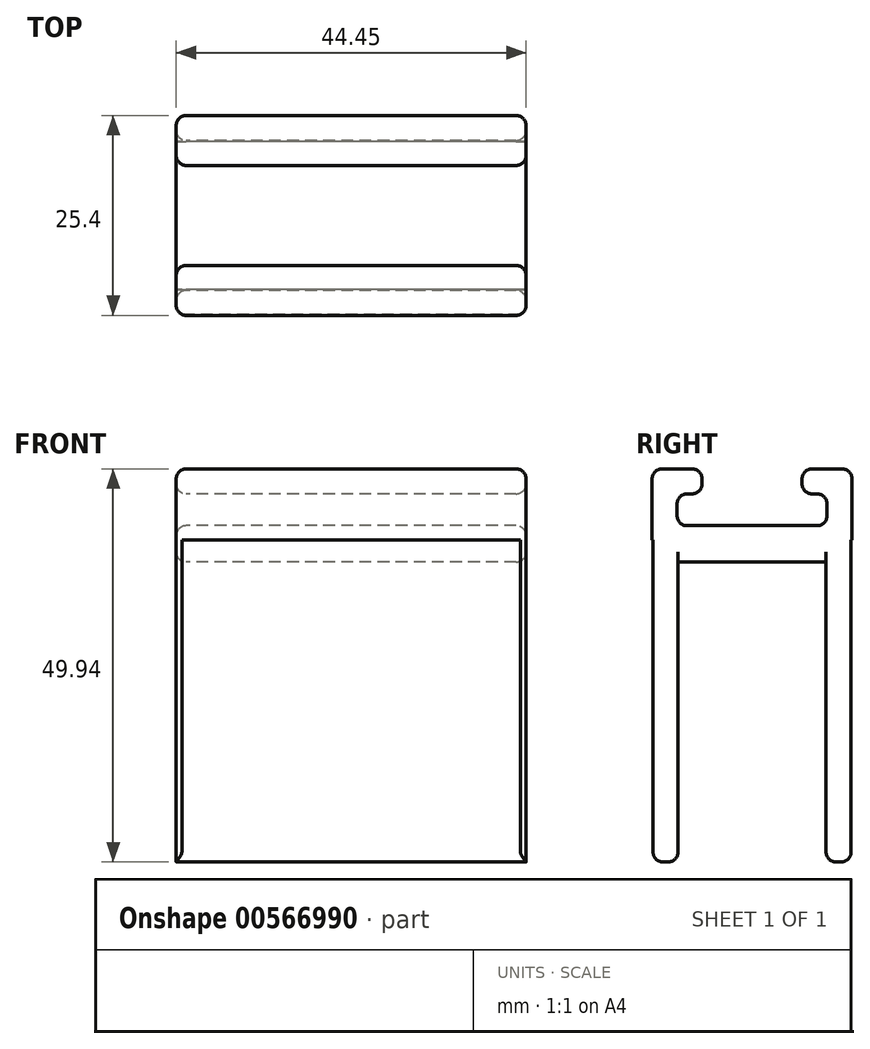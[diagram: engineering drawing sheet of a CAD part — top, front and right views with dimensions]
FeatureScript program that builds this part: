
annotation { "Feature Type Name" : "Feature", "Feature Type Description" : "" }
export const myFeature = defineFeature(function(context is Context, id is Id, definition is map)
    precondition{}
    {
        {
            var Q0;
            Q0=qCreatedBy(makeId("Right.planeOp"),FACE);
            var sketch = newSketch(context, id + "F0", { "sketchPlane" : qUnion([Q0])});
            skLineSegment(sketch, "E0.bottom", {"start": v(11.3, -24.97) * mm, "end": v(10.67, -24.97) * mm});
            skLineSegment(sketch, "E0.top", {"start": v(11.43, 24.97) * mm, "end": v(7.62, 24.97) * mm});
            skLineSegment(sketch, "E0.left", {"start": v(12.57, -23.7) * mm, "end": v(12.57, 15.95) * mm});
            skLineSegment(sketch, "E0.right", {"start": v(-12.57, -23.7) * mm, "end": v(-12.57, 15.95) * mm});
            skPoint(sketch, "E0.middle", {"position": v(0, 0) * mm});
            skLineSegment(sketch, "E1.top", {"start": v(-9.4, 13.13) * mm, "end": v(9.4, 13.13) * mm});
            skLineSegment(sketch, "E1.left", {"start": v(-9.4, -23.7) * mm, "end": v(-9.4, 13.13) * mm});
            skLineSegment(sketch, "E1.right", {"start": v(9.4, -23.7) * mm, "end": v(9.4, 13.13) * mm});
            skLineSegment(sketch, "E2.trimOffspring", {"start": v(-10.67, -24.97) * mm, "end": v(-11.3, -24.97) * mm});
            skLineSegment(sketch, "E3.bottom", {"start": v(8.26, 17.75) * mm, "end": v(-8.26, 17.75) * mm});
            skLineSegment(sketch, "E3.top", {"start": v(8.26, 21.8) * mm, "end": v(7.62, 21.8) * mm});
            skLineSegment(sketch, "E3.left", {"start": v(9.53, 19.02) * mm, "end": v(9.53, 20.52) * mm});
            skLineSegment(sketch, "E3.right", {"start": v(-9.53, 19.02) * mm, "end": v(-9.53, 20.52) * mm});
            skPoint(sketch, "E3.middle", {"position": v(0, 19.77) * mm});
            skPoint(sketch, "E3.middle.positionSnap0", {"position": v(0, 13.13) * mm});
            skPoint(sketch, "E3.centerSnap0", {"position": v(0, 13.13) * mm});
            skLineSegment(sketch, "E4.left", {"start": v(6.35, 23.7) * mm, "end": v(6.35, 23.06) * mm});
            skLineSegment(sketch, "E4.right", {"start": v(-6.35, 23.7) * mm, "end": v(-6.35, 23.06) * mm});
            skPoint(sketch, "E4.middle", {"position": v(0, 21.8) * mm});
            skLineSegment(sketch, "E5.trimOffspring", {"start": v(-7.62, 21.8) * mm, "end": v(-8.26, 21.8) * mm});
            skLineSegment(sketch, "E6.trimOffspring", {"start": v(-7.62, 24.97) * mm, "end": v(-11.43, 24.97) * mm});
            skPoint(sketch, "E4.top.end.orphan", {"position": v(-6.35, 18.62) * mm});
            skPoint(sketch, "E7.orphan", {"position": v(6.35, 18.62) * mm});
            skLineSegment(sketch, "E8.top", {"start": v(-12.7, 15.95) * mm, "end": v(-12.57, 15.95) * mm});
            skLineSegment(sketch, "E8.right", {"start": v(-12.7, 23.7) * mm, "end": v(-12.7, 15.95) * mm});
            skPoint(sketch, "E9.orphan", {"position": v(-12.57, 24.97) * mm});
            skLineSegment(sketch, "E10.top", {"start": v(12.7, 15.95) * mm, "end": v(12.57, 15.95) * mm});
            skLineSegment(sketch, "E10.right", {"start": v(12.7, 23.7) * mm, "end": v(12.7, 15.95) * mm});
            skPoint(sketch, "E11.orphan", {"position": v(12.57, 24.97) * mm});
            skPoint(sketch, "E12.visualSharp", {"position": v(-6.35, 21.8) * mm});
            skArc(sketch, "E12.filletArc", {"start": v(-7.62, 21.8) * mm, "mid": v(-6.72, 22.16) * mm, "end": v(-6.35, 23.06) * mm});
            skPoint(sketch, "E13.visualSharp", {"position": v(6.35, 21.8) * mm});
            skArc(sketch, "E13.filletArc", {"start": v(6.35, 23.06) * mm, "mid": v(6.72, 22.16) * mm, "end": v(7.62, 21.8) * mm});
            skPoint(sketch, "E14.visualSharp", {"position": v(6.35, 24.97) * mm});
            skArc(sketch, "E14.filletArc", {"start": v(7.62, 24.97) * mm, "mid": v(6.72, 24.6) * mm, "end": v(6.35, 23.7) * mm});
            skPoint(sketch, "E15.visualSharp", {"position": v(-6.35, 24.97) * mm});
            skArc(sketch, "E15.filletArc", {"start": v(-6.35, 23.7) * mm, "mid": v(-6.72, 24.6) * mm, "end": v(-7.62, 24.97) * mm});
            skPoint(sketch, "E16.visualSharp", {"position": v(-12.7, 24.97) * mm});
            skArc(sketch, "E16.filletArc", {"start": v(-11.43, 24.97) * mm, "mid": v(-12.33, 24.6) * mm, "end": v(-12.7, 23.7) * mm});
            skPoint(sketch, "E17.visualSharp", {"position": v(12.7, 24.97) * mm});
            skArc(sketch, "E17.filletArc", {"start": v(12.7, 23.7) * mm, "mid": v(12.33, 24.6) * mm, "end": v(11.43, 24.97) * mm});
            skPoint(sketch, "E18.visualSharp", {"position": v(-9.53, 17.75) * mm});
            skArc(sketch, "E18.filletArc", {"start": v(-9.53, 19.02) * mm, "mid": v(-9.15, 18.13) * mm, "end": v(-8.26, 17.75) * mm});
            skPoint(sketch, "E19.visualSharp", {"position": v(9.53, 17.75) * mm});
            skArc(sketch, "E19.filletArc", {"start": v(8.26, 17.75) * mm, "mid": v(9.15, 18.13) * mm, "end": v(9.52, 19.02) * mm});
            skPoint(sketch, "E20.visualSharp", {"position": v(12.57, 15.95) * mm});
            skPoint(sketch, "E21.visualSharp", {"position": v(-12.7, 15.95) * mm});
            skPoint(sketch, "E22.visualSharp", {"position": v(-12.57, 15.95) * mm});
            skPoint(sketch, "E23.visualSharp", {"position": v(-12.57, -24.97) * mm});
            skArc(sketch, "E23.filletArc", {"start": v(-12.57, -23.7) * mm, "mid": v(-12.2, -24.6) * mm, "end": v(-11.3, -24.97) * mm});
            skPoint(sketch, "E24.visualSharp", {"position": v(-9.4, -24.97) * mm});
            skArc(sketch, "E24.filletArc", {"start": v(-10.67, -24.97) * mm, "mid": v(-9.77, -24.6) * mm, "end": v(-9.4, -23.7) * mm});
            skPoint(sketch, "E25.visualSharp", {"position": v(9.4, -24.97) * mm});
            skArc(sketch, "E25.filletArc", {"start": v(9.4, -23.7) * mm, "mid": v(9.77, -24.6) * mm, "end": v(10.67, -24.97) * mm});
            skPoint(sketch, "E26.visualSharp", {"position": v(12.57, -24.97) * mm});
            skArc(sketch, "E26.filletArc", {"start": v(11.3, -24.97) * mm, "mid": v(12.2, -24.6) * mm, "end": v(12.57, -23.7) * mm});
            skPoint(sketch, "E27.visualSharp", {"position": v(-9.53, 21.8) * mm});
            skArc(sketch, "E27.filletArc", {"start": v(-8.26, 21.8) * mm, "mid": v(-9.15, 21.42) * mm, "end": v(-9.53, 20.52) * mm});
            skPoint(sketch, "E28.visualSharp", {"position": v(9.53, 21.8) * mm});
            skArc(sketch, "E28.filletArc", {"start": v(9.53, 20.52) * mm, "mid": v(9.15, 21.42) * mm, "end": v(8.26, 21.8) * mm});
            skSolve(sketch);
        }
        {
            var Q0;
            Q0 = qSketchRegion(id + "F0", true);
            extrude(context, id + "F1", {"entities" : qUnion([Q0]), "depth" : 44.45 * mm, "offsetDistance" : 25.4 * mm});
        }
        {
            var Q0;
            Q0=makeQuery(id+"F1.opExtrude","CAP_EDGE",EDGE,{"disambiguationData":[OSD([sQuery(id+"F0.wireOp",EDGE,"E8.right")])],"isStart":false});
            var Q1;
            Q1=makeQuery(id+"F1.opExtrude","CAP_EDGE",EDGE,{"disambiguationData":[OSD([sQuery(id+"F0.wireOp",EDGE,"E6.trimOffspring")])],"isStart":false});
            var Q2;
            Q2=makeQuery(id+"F1.opExtrude","CAP_EDGE",EDGE,{"disambiguationData":[OSD([sQuery(id+"F0.wireOp",EDGE,"E3.bottom")])],"isStart":true});
            var Q3;
            Q3=makeQuery(id+"F1.opExtrude","CAP_EDGE",EDGE,{"disambiguationData":[OSD([sQuery(id+"F0.wireOp",EDGE,"E1.top")])],"isStart":true});
            var Q4;
            Q4=makeQuery(id+"F1.opExtrude","CAP_EDGE",EDGE,{"disambiguationData":[OSD([sQuery(id+"F0.wireOp",EDGE,"E1.top")])],"isStart":false});
            fillet(context, id + "F2", {"entities" : qUnion([Q0, Q1, Q2, Q3, Q4]), "radius" : 1.27 * mm, "tangentPropagation" : true, "allowEdgeOverflow" : false});
        }
    });
